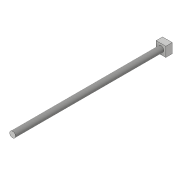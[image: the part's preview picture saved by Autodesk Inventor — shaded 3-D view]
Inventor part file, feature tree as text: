
AUTODESK INVENTOR PART (.ipt)
format: ipt  version: 2019 (Build 230136000, 136)  size: 93,696 bytes
history: native  units: in
note: dims shown in document units (in); Inventor stores cm internally (conversion verified against a paired STEP export)
features: sketch x4, extrude x3, thread x2, plane x1
ambient origin geometry x8: Origin, YZ Plane, XZ Plane, XY Plane, X Axis, Y Axis, Z Axis, Center Point
bodies: Solid1 (feature_tree)
feature tree (10):
  extrude  "Extrusion1"  Depth=0.5906in
  extrude  "Extrusion2"  Depth=9.0551in TaperAngle=0.0deg
  thread  "Thread1"  [1 undecoded]
  thread  "Thread2"  [1 undecoded]
  sketch  "Sketch3"  dims[d10=0.3937in d11=0.0in d12=0.0in]
  plane  "Work Plane1"
  extrude  "Extrusion3"  TaperAngle=0.0deg  [1 undecoded]
  sketch  "Sketch1"  dims[d0=0.5906in d1=0.5906in]
  sketch  "Sketch2"  dims[d2=0.3937in d3=0.0in d5=9.0551in d6=0.0in d7=0.3937in d8=0.0in d9=0.3543in]
  sketch  "Sketch4"  dims[d14=0.7874in d15=0.0in]
note: 3 required parameter values undecoded (feature->parameter linkage not recoverable at this tier; creation-order binding heuristic only, values carry confidence <= 0.55)
